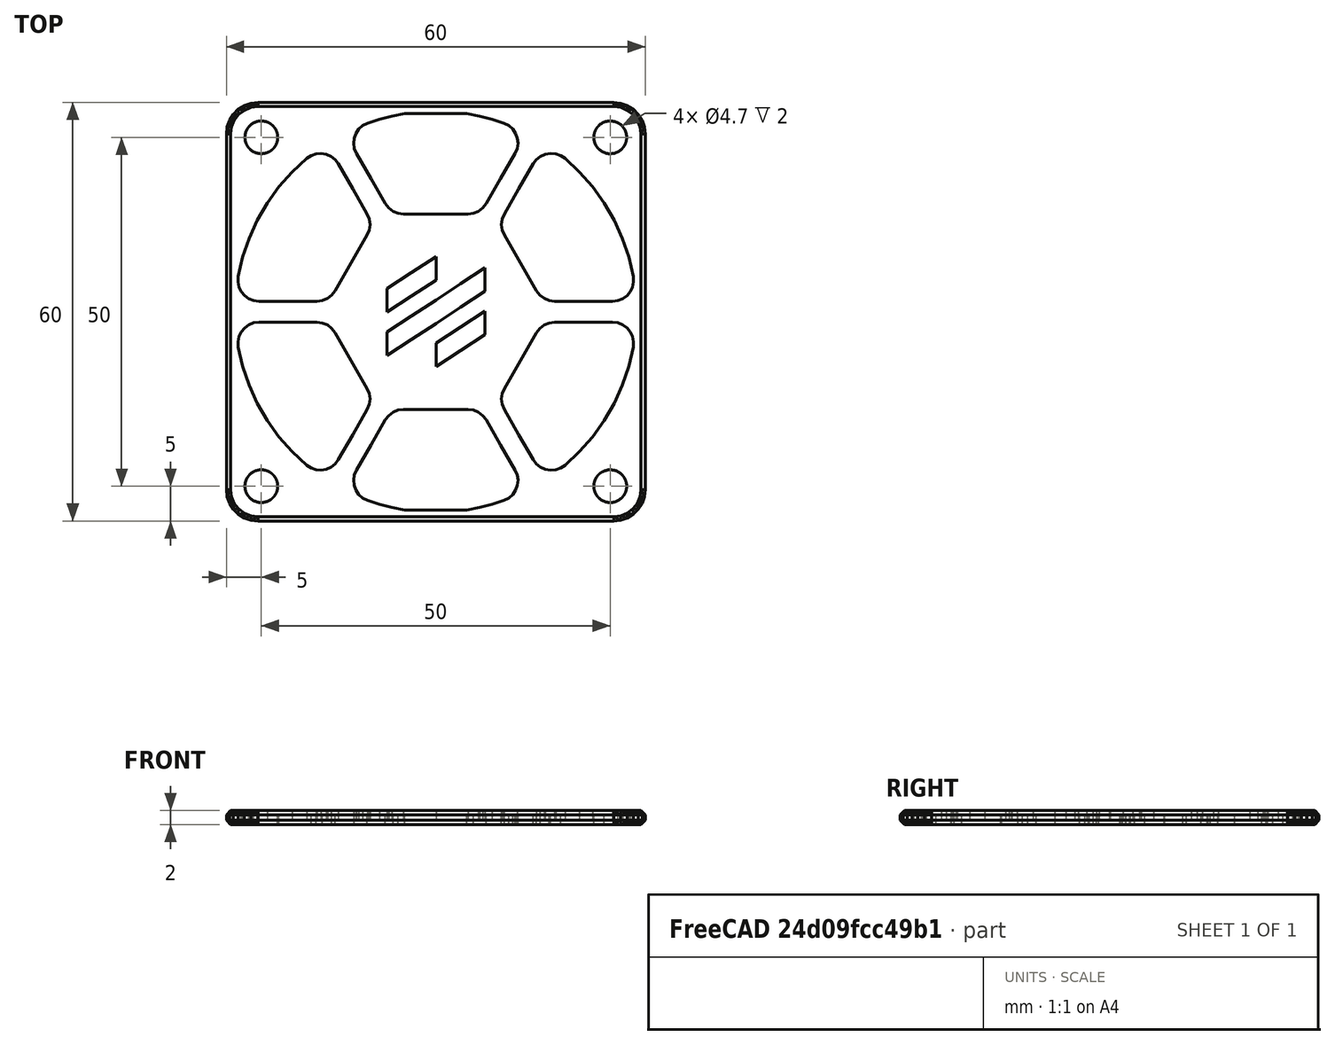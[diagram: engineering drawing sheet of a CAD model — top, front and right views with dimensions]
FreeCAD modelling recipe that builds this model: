
FCSTD DOCUMENT  (FreeCAD 0.18R16146 (Git))
Label: fan-guard
License: Other
LicenseURL: GPL3
objects: Part::Cylinder×5, Part::Feature×1, Part::MultiCommon×1, Part::MultiFuse×1, Part::Cut×1
note: 9 computed .brp shape members not serialized (recipe doc carries the construction recipe); baked Part::Feature solids carry a one-line shape summary decoded from their .brp

FEATURE [Part::Feature] _0mm_fan_grill_rev1001001_solid  label="_0mm_fan_grill_rev1002 (Solid)"
  Placement = pos=(-9,-227,0) rot=(0,0,1;0rad)
  shape: bbox 60 x 60 x 22 mm, 1461 faces (baked)
FEATURE [Part::Cylinder] Cylinder
  Angle = 360
  AttacherType = Attacher::AttachEngine3D
  Height = 5
  Radius = 46
FEATURE [Part::MultiCommon] Common
  Shapes = -> [Cylinder,_0mm_fan_grill_rev1001001_solid]
FEATURE [Part::Cylinder] Cylinder001
  Angle = 360
  AttacherType = Attacher::AttachEngine3D
  Height = 10
  Placement = pos=(-25,25,0) rot=(0,0,1;0rad)
  Radius = 2.35
FEATURE [Part::Cylinder] Cylinder002
  Angle = 360
  AttacherType = Attacher::AttachEngine3D
  Height = 10
  Placement = pos=(25,-25,0) rot=(0,0,1;0rad)
  Radius = 2.35
FEATURE [Part::Cylinder] Cylinder003
  Angle = 360
  AttacherType = Attacher::AttachEngine3D
  Height = 10
  Placement = pos=(-25,-25,0) rot=(0,0,1;0rad)
  Radius = 2.35
FEATURE [Part::Cylinder] Cylinder004
  Angle = 360
  AttacherType = Attacher::AttachEngine3D
  Height = 10
  Placement = pos=(25,25,0) rot=(0,0,1;0rad)
  Radius = 2.35
FEATURE [Part::MultiFuse] Fusion
  Shapes = -> [Cylinder004,Cylinder003,Cylinder001,Cylinder002]
FEATURE [Part::Cut] Cut
  Base = -> Common
  Tool = -> Fusion
